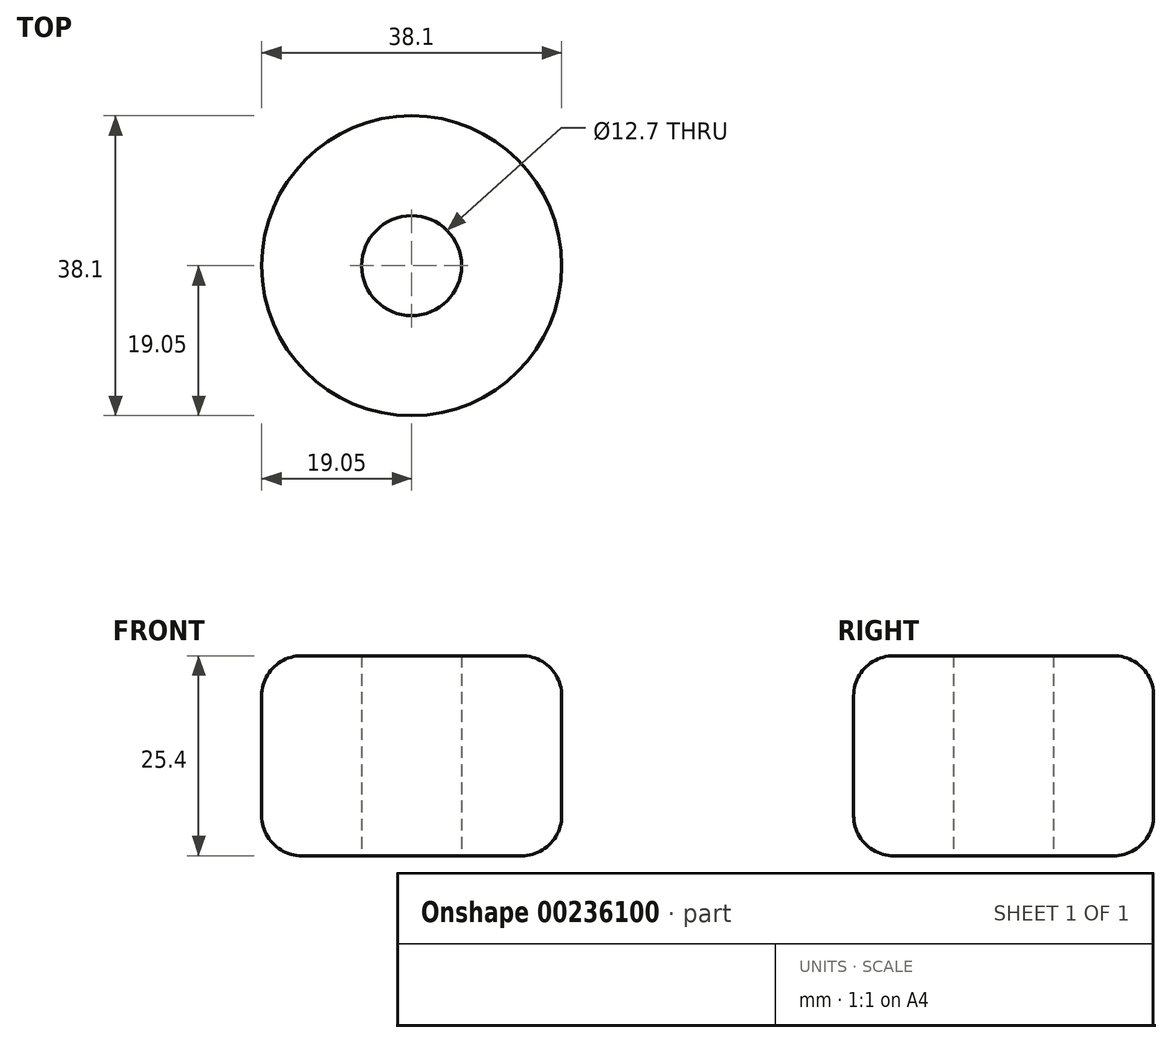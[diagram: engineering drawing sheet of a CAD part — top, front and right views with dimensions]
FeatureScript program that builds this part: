
annotation { "Feature Type Name" : "Feature", "Feature Type Description" : "" }
export const myFeature = defineFeature(function(context is Context, id is Id, definition is map)
    precondition{}
    {
        {
            var Q0;
            Q0=qCreatedBy(makeId("Top.planeOp"),FACE);
            var sketch = newSketch(context, id + "F0", { "sketchPlane" : qUnion([Q0])});
            skCircle(sketch, "E0", {"center": v(0, 0) * mm, "radius": 19.05 * mm});
            skCircle(sketch, "E1", {"center": v(0, 0) * mm, "radius": 6.35 * mm});
            skSolve(sketch);
        }
        {
            var Q0;
            Q0 = qSketchRegion(id + "F0", true);
            extrude(context, id + "F1", {"entities" : qUnion([Q0]), "endBound" : BoundingType.SYMMETRIC, "depth" : 25.4 * mm});
        }
        {
            var Q0;
            Q0=makeQuery(id+"F1.opExtrude","CAP_EDGE",EDGE,{"disambiguationData":[OSD([sQuery(id+"F0.wireOp",EDGE,"E0")])],"isStart":false});
            var Q1;
            Q1=makeQuery(id+"F1.opExtrude","CAP_EDGE",EDGE,{"disambiguationData":[OSD([sQuery(id+"F0.wireOp",EDGE,"E0")])],"isStart":true});
            fillet(context, id + "F2", {"entities" : qUnion([Q0, Q1]), "radius" : 5.08 * mm, "tangentPropagation" : true, "allowEdgeOverflow" : false});
        }
    });
